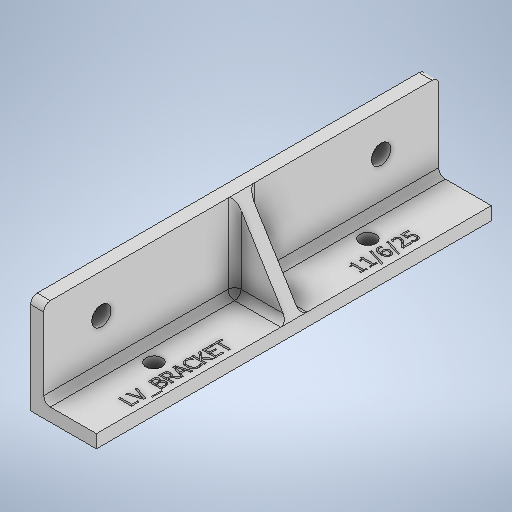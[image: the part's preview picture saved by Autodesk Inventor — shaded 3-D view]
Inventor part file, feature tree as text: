
AUTODESK INVENTOR PART (.ipt)
format: ipt  version: 2025 (Build 290162000, 162)  size: 639,488 bytes
history: native  units: in
note: dims shown in document units (in); Inventor stores cm internally (conversion verified against a paired STEP export)
features: sketch x6, extrude x3, fillet x2, hole x2, mirror x2, other x1
ambient origin geometry x8: Origin, YZ Plane, XZ Plane, XY Plane, X Axis, Y Axis, Z Axis, Center Point
bodies: Solid1 (feature_tree)
feature tree (16):
  extrude  "Base"  Depth=0.7874in
  extrude  "Center Truss"  Depth=0.1575in
  fillet  "Fillet1"  Radius=4.7244in
  hole  "LV Mount Hole"  [1 undecoded]
  mirror  "Mirror1"
  hole  "80/20 Mount Hole"  [1 undecoded]
  mirror  "Mirror2"
  extrude  "Alignment Pins"  Depth=0.0394in
  fillet  "Fillet2"  Radius=1.2795in
  other  "LABEL"
  sketch  "Sketch1"  dims[d0=1.1811in d1=0.7874in]
  sketch  "Sketch2"  dims[d2=0.1575in d3=0.1575in d4=4.7244in d5=0.0in]
  sketch  "Sketch3"  dims[d6=0.1575in d7=0.0in d11=0.0787in]
  sketch  "Sketch4"  dims[d12=0.2323in d13=0.2362in d14=0.1575in d15=0.0787in d16=90.0deg d17=0.315in d18=0.8108in d19=0.7197in]
  sketch  "Sketch5"  dims[d20=1.6732in]
  sketch  "Sketch6"  dims[d21=0.1929in d22=0.2362in d23=0.1575in d24=0.0787in d25=90.0deg d26=0.315in d27=0.8108in d28=0.3937in d29=1.2795in d31=0.1457in d32=1.2205in d33=0.1457in d34=0.4724in d35=0.1181in d36=0.0in d37=0.0394in d38=0.0394in d39=0.0in d30=0.0025in d40=0.0in d41=0.0in]
note: 2 required parameter values undecoded (feature->parameter linkage not recoverable at this tier; creation-order binding heuristic only, values carry confidence <= 0.55)
